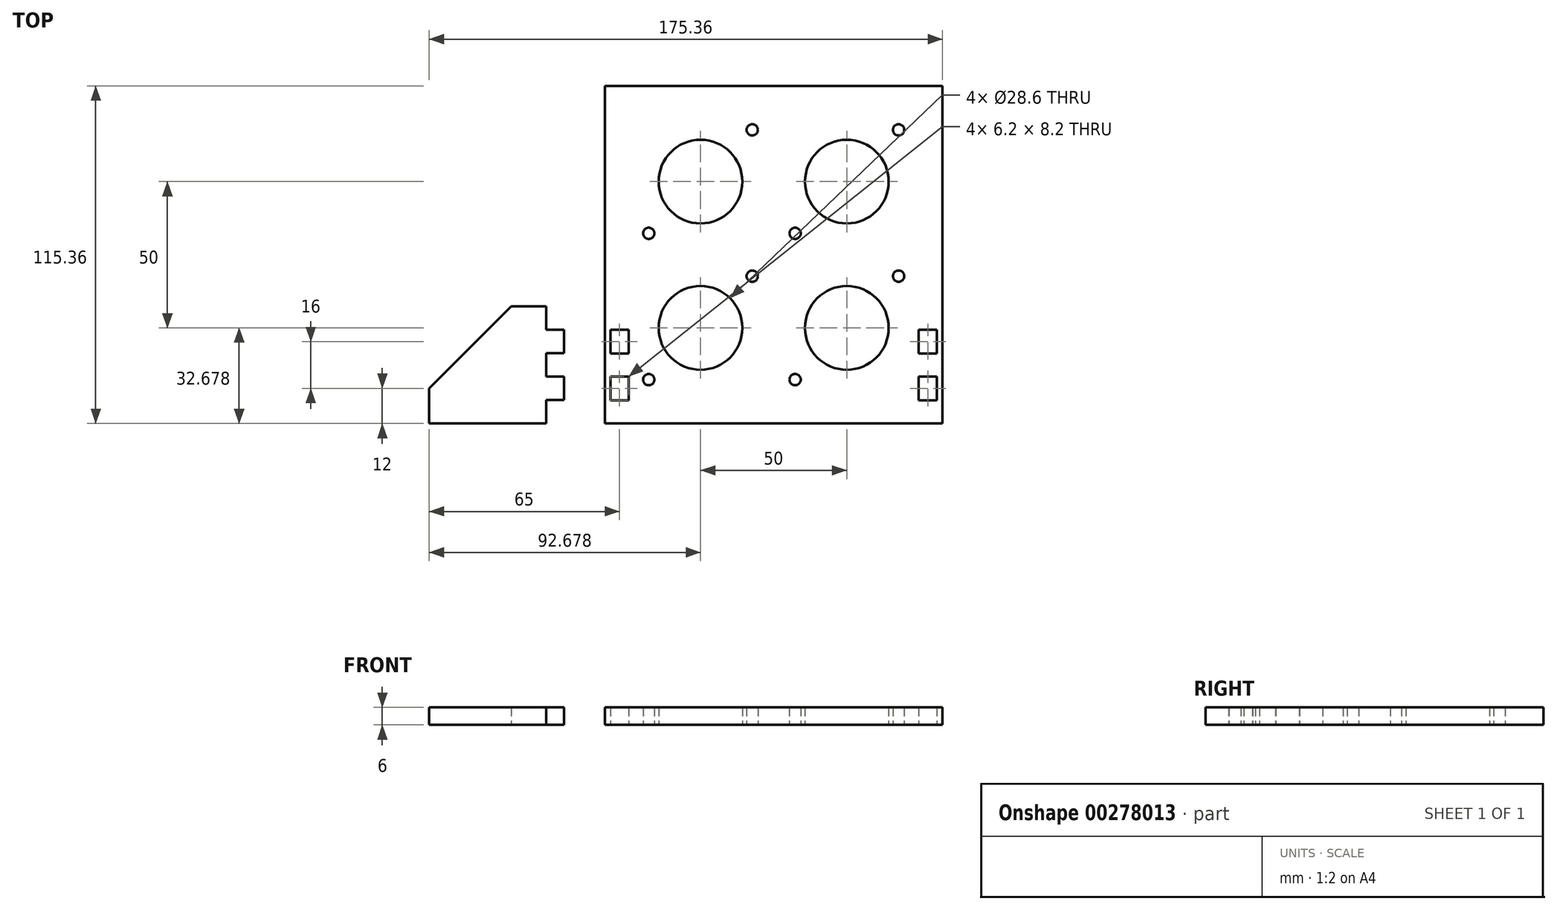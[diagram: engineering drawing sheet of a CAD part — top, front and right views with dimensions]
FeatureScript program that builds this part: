
annotation { "Feature Type Name" : "Feature", "Feature Type Description" : "" }
export const myFeature = defineFeature(function(context is Context, id is Id, definition is map)
    precondition{}
    {
        {
            assignVariable(context, id + "F0", {"name" : "X", "anyValue" : 6 * mm});
        }
        {
            var Q0;
            Q0=qCreatedBy(makeId("Top.planeOp"),FACE);
            var sketch = newSketch(context, id + "F1", { "sketchPlane" : qUnion([Q0])});
            skCircle(sketch, "E0", {"center": v(32.68, 32.68) * mm, "radius": 13.5 * mm, "construction": true});
            skCircle(sketch, "E1", {"center": v(15, 15) * mm, "radius": 1.93 * mm});
            skCircle(sketch, "E2", {"center": v(32.68, 32.68) * mm, "radius": 14.3 * mm});
            skCircle(sketch, "E3", {"center": v(50.36, 50.36) * mm, "radius": 1.93 * mm});
            skLineSegment(sketch, "E4", {"start": v(15, 15) * mm, "end": v(50.36, 50.36) * mm, "construction": true});
            skCircle(sketch, "E5.0.1.0", {"center": v(50.36, 100.36) * mm, "radius": 1.93 * mm});
            skCircle(sketch, "E5.0.1.1", {"center": v(32.68, 82.68) * mm, "radius": 14.3 * mm});
            skCircle(sketch, "E5.0.1.2", {"center": v(15, 65) * mm, "radius": 1.93 * mm});
            skCircle(sketch, "E5.1.0.0", {"center": v(100.36, 50.36) * mm, "radius": 1.93 * mm});
            skCircle(sketch, "E5.1.0.1", {"center": v(82.68, 32.68) * mm, "radius": 14.3 * mm});
            skCircle(sketch, "E5.1.0.2", {"center": v(65, 15) * mm, "radius": 1.93 * mm});
            skCircle(sketch, "E5.1.1.0", {"center": v(100.36, 100.36) * mm, "radius": 1.93 * mm});
            skCircle(sketch, "E5.1.1.1", {"center": v(82.68, 82.68) * mm, "radius": 14.3 * mm});
            skCircle(sketch, "E5.1.1.2", {"center": v(65, 65) * mm, "radius": 1.93 * mm});
            skLineSegment(sketch, "E5.direction1", {"start": v(15, 15) * mm, "end": v(65, 15) * mm, "construction": true});
            skLineSegment(sketch, "E5.direction2", {"start": v(15, 15) * mm, "end": v(15, 65) * mm, "construction": true});
            skLineSegment(sketch, "E6.bottom", {"start": v(0, 0) * mm, "end": v(115.36, 0) * mm});
            skLineSegment(sketch, "E7", {"start": v(100.36, 100.36) * mm, "end": v(100.36, 115.36) * mm, "construction": true});
            skLineSegment(sketch, "E8", {"start": v(100.36, 100.36) * mm, "end": v(115.36, 100.36) * mm, "construction": true});
            skLineSegment(sketch, "E9", {"start": v(15, 15) * mm, "end": v(0, 15) * mm, "construction": true});
            skLineSegment(sketch, "E10", {"start": v(15, 15) * mm, "end": v(15, 0) * mm, "construction": true});
            skLineSegment(sketch, "E11", {"start": v(-32, 40) * mm, "end": v(-60, 12) * mm});
            skLineSegment(sketch, "E12", {"start": v(-60, 12) * mm, "end": v(-60, 0) * mm});
            skLineSegment(sketch, "E13", {"start": v(-60, 0) * mm, "end": v(-20, 0) * mm});
            skLineSegment(sketch, "E14", {"start": v(-20, 0) * mm, "end": v(-20, 8) * mm});
            skLineSegment(sketch, "E15", {"start": v(-20, 40) * mm, "end": v(-32, 40) * mm});
            skLineSegment(sketch, "E16.trimOffspring", {"start": v(0, 0) * mm, "end": v(0, 115.36) * mm});
            skLineSegment(sketch, "E17", {"start": v(57.68, 115.36) * mm, "end": v(57.68, 0) * mm, "construction": true});
            skLineSegment(sketch, "E18", {"start": v(65, 10) * mm, "end": v(88.28, 10) * mm, "construction": true});
            skLineSegment(sketch, "E19", {"start": v(88.28, 10) * mm, "end": v(106.1, 27.82) * mm, "construction": true});
            skLineSegment(sketch, "E20", {"start": v(106.1, 27.82) * mm, "end": v(106.1, 51.1) * mm, "construction": true});
            skLineSegment(sketch, "E21", {"start": v(101.1, 56.1) * mm, "end": v(77.82, 56.1) * mm, "construction": true});
            skLineSegment(sketch, "E22", {"start": v(77.82, 56.1) * mm, "end": v(60, 38.28) * mm, "construction": true});
            skLineSegment(sketch, "E23", {"start": v(60, 38.28) * mm, "end": v(60, 15) * mm, "construction": true});
            skPoint(sketch, "E24.visualSharp", {"position": v(106.1, 56.1) * mm});
            skArc(sketch, "E24.filletArc", {"start": v(106.1, 51.1) * mm, "mid": v(104.64, 54.64) * mm, "end": v(101.1, 56.1) * mm, "construction": true});
            skPoint(sketch, "E25.visualSharp", {"position": v(60, 10) * mm});
            skArc(sketch, "E25.filletArc", {"start": v(60, 15) * mm, "mid": v(61.46, 11.46) * mm, "end": v(65, 10) * mm, "construction": true});
            skLineSegment(sketch, "E26", {"start": v(60, 10) * mm, "end": v(154.26, 104.26) * mm, "construction": true});
            skLineSegment(sketch, "E27", {"start": v(106.1, 56.1) * mm, "end": v(200.36, 150.36) * mm, "construction": true});
            skLineSegment(sketch, "E28", {"start": v(154.26, 104.26) * mm, "end": v(200.36, 150.36) * mm, "construction": true});
            skPoint(sketch, "E29", {"position": v(61.46, 11.46) * mm});
            skPoint(sketch, "E30", {"position": v(104.64, 54.64) * mm});
            skLineSegment(sketch, "E31.0.1.0", {"start": v(106.1, 77.82) * mm, "end": v(106.1, 101.1) * mm, "construction": true});
            skArc(sketch, "E31.0.1.1", {"start": v(106.1, 101.1) * mm, "mid": v(104.64, 104.64) * mm, "end": v(101.1, 106.1) * mm, "construction": true});
            skLineSegment(sketch, "E31.0.1.2", {"start": v(101.1, 106.1) * mm, "end": v(77.82, 106.1) * mm, "construction": true});
            skLineSegment(sketch, "E31.0.1.3", {"start": v(77.82, 106.1) * mm, "end": v(60, 88.28) * mm, "construction": true});
            skLineSegment(sketch, "E31.0.1.4", {"start": v(60, 88.28) * mm, "end": v(60, 65) * mm, "construction": true});
            skArc(sketch, "E31.0.1.5", {"start": v(60, 65) * mm, "mid": v(61.46, 61.46) * mm, "end": v(65, 60) * mm, "construction": true});
            skLineSegment(sketch, "E31.0.1.6", {"start": v(65, 60) * mm, "end": v(88.28, 60) * mm, "construction": true});
            skLineSegment(sketch, "E31.0.1.7", {"start": v(88.28, 60) * mm, "end": v(106.1, 77.82) * mm, "construction": true});
            skLineSegment(sketch, "E31.1.0.0", {"start": v(56.1, 27.82) * mm, "end": v(56.1, 51.1) * mm, "construction": true});
            skArc(sketch, "E31.1.0.1", {"start": v(56.1, 51.1) * mm, "mid": v(54.64, 54.64) * mm, "end": v(51.1, 56.1) * mm, "construction": true});
            skLineSegment(sketch, "E31.1.0.2", {"start": v(51.1, 56.1) * mm, "end": v(27.82, 56.1) * mm, "construction": true});
            skLineSegment(sketch, "E31.1.0.3", {"start": v(27.82, 56.1) * mm, "end": v(10, 38.28) * mm, "construction": true});
            skLineSegment(sketch, "E31.1.0.4", {"start": v(10, 38.28) * mm, "end": v(10, 15) * mm, "construction": true});
            skArc(sketch, "E31.1.0.5", {"start": v(10, 15) * mm, "mid": v(11.46, 11.46) * mm, "end": v(15, 10) * mm, "construction": true});
            skLineSegment(sketch, "E31.1.0.6", {"start": v(15, 10) * mm, "end": v(38.28, 10) * mm, "construction": true});
            skLineSegment(sketch, "E31.1.0.7", {"start": v(38.28, 10) * mm, "end": v(56.1, 27.82) * mm, "construction": true});
            skLineSegment(sketch, "E31.1.1.0", {"start": v(56.1, 77.82) * mm, "end": v(56.1, 101.1) * mm, "construction": true});
            skArc(sketch, "E31.1.1.1", {"start": v(56.1, 101.1) * mm, "mid": v(54.64, 104.64) * mm, "end": v(51.1, 106.1) * mm, "construction": true});
            skLineSegment(sketch, "E31.1.1.2", {"start": v(51.1, 106.1) * mm, "end": v(27.82, 106.1) * mm, "construction": true});
            skLineSegment(sketch, "E31.1.1.3", {"start": v(27.82, 106.1) * mm, "end": v(10, 88.28) * mm, "construction": true});
            skLineSegment(sketch, "E31.1.1.4", {"start": v(10, 88.28) * mm, "end": v(10, 65) * mm, "construction": true});
            skArc(sketch, "E31.1.1.5", {"start": v(10, 65) * mm, "mid": v(11.46, 61.46) * mm, "end": v(15, 60) * mm, "construction": true});
            skLineSegment(sketch, "E31.1.1.6", {"start": v(15, 60) * mm, "end": v(38.28, 60) * mm, "construction": true});
            skLineSegment(sketch, "E31.1.1.7", {"start": v(38.28, 60) * mm, "end": v(56.1, 77.82) * mm, "construction": true});
            skLineSegment(sketch, "E31.direction1", {"start": v(65, 10) * mm, "end": v(15, 10) * mm, "construction": true});
            skLineSegment(sketch, "E31.direction2", {"start": v(65, 10) * mm, "end": v(65, 60) * mm, "construction": true});
            skLineSegment(sketch, "E32.trimOffspring", {"start": v(0, 115.36) * mm, "end": v(115.36, 115.36) * mm});
            skLineSegment(sketch, "E33", {"start": v(115.36, 0) * mm, "end": v(115.36, 115.36) * mm});
            skLineSegment(sketch, "E34", {"start": v(-20, 32) * mm, "end": v(-14, 32) * mm});
            skLineSegment(sketch, "E35", {"start": v(-14, 32) * mm, "end": v(-14, 24) * mm});
            skLineSegment(sketch, "E36", {"start": v(-14, 24) * mm, "end": v(-20, 24) * mm});
            skLineSegment(sketch, "E37", {"start": v(-20, 16) * mm, "end": v(-14, 16) * mm});
            skLineSegment(sketch, "E38", {"start": v(-14, 16) * mm, "end": v(-14, 8) * mm});
            skLineSegment(sketch, "E39", {"start": v(-14, 8) * mm, "end": v(-20, 8) * mm});
            skLineSegment(sketch, "E40.trimOffspring", {"start": v(-20, 32) * mm, "end": v(-20, 40) * mm});
            skLineSegment(sketch, "E41.trimOffspring", {"start": v(-20, 16) * mm, "end": v(-20, 24) * mm});
            skLineSegment(sketch, "E42.bottom", {"start": v(2, 16) * mm, "end": v(8, 16) * mm, "construction": true});
            skLineSegment(sketch, "E42.top", {"start": v(2, 8) * mm, "end": v(8, 8) * mm, "construction": true});
            skLineSegment(sketch, "E42.left", {"start": v(2, 16) * mm, "end": v(2, 8) * mm, "construction": true});
            skLineSegment(sketch, "E42.right", {"start": v(8, 16) * mm, "end": v(8, 8) * mm, "construction": true});
            skLineSegment(sketch, "E43.bottom", {"start": v(2, 32) * mm, "end": v(8, 32) * mm, "construction": true});
            skLineSegment(sketch, "E43.top", {"start": v(2, 24) * mm, "end": v(8, 24) * mm, "construction": true});
            skLineSegment(sketch, "E43.left", {"start": v(2, 32) * mm, "end": v(2, 24) * mm, "construction": true});
            skLineSegment(sketch, "E43.right", {"start": v(8, 32) * mm, "end": v(8, 24) * mm, "construction": true});
            skLineSegment(sketch, "E44", {"start": v(10, 15.9) * mm, "end": v(8, 15.9) * mm, "construction": true});
            skLineSegment(sketch, "E45", {"start": v(2, 15.45) * mm, "end": v(0, 15.45) * mm, "construction": true});
            skLineSegment(sketch, "E46.0", {"start": v(1.9, 23.9) * mm, "end": v(8.1, 23.9) * mm});
            skLineSegment(sketch, "E46.1", {"start": v(1.9, 32.1) * mm, "end": v(1.9, 23.9) * mm});
            skLineSegment(sketch, "E46.2", {"start": v(1.9, 32.1) * mm, "end": v(8.1, 32.1) * mm});
            skLineSegment(sketch, "E46.3", {"start": v(8.1, 32.1) * mm, "end": v(8.1, 23.9) * mm});
            skLineSegment(sketch, "E47.0", {"start": v(1.9, 16.1) * mm, "end": v(1.9, 7.9) * mm});
            skLineSegment(sketch, "E47.1", {"start": v(1.9, 16.1) * mm, "end": v(8.1, 16.1) * mm});
            skLineSegment(sketch, "E47.2", {"start": v(8.1, 16.1) * mm, "end": v(8.1, 7.9) * mm});
            skLineSegment(sketch, "E47.3", {"start": v(1.9, 7.9) * mm, "end": v(8.1, 7.9) * mm});
            skLineSegment(sketch, "E48.MirrorCS", {"start": v(107.26, 32.1) * mm, "end": v(107.26, 23.9) * mm});
            skLineSegment(sketch, "E49.MirrorCS", {"start": v(113.46, 32.1) * mm, "end": v(107.26, 32.1) * mm});
            skLineSegment(sketch, "E50.MirrorCS", {"start": v(113.46, 32.1) * mm, "end": v(113.46, 23.9) * mm});
            skLineSegment(sketch, "E51.MirrorCS", {"start": v(113.46, 23.9) * mm, "end": v(107.26, 23.9) * mm});
            skLineSegment(sketch, "E52.MirrorCS", {"start": v(107.26, 16.1) * mm, "end": v(107.26, 7.9) * mm});
            skLineSegment(sketch, "E53.MirrorCS", {"start": v(113.46, 7.9) * mm, "end": v(107.26, 7.9) * mm});
            skLineSegment(sketch, "E54.MirrorCS", {"start": v(113.46, 16.1) * mm, "end": v(107.26, 16.1) * mm});
            skLineSegment(sketch, "E55.MirrorCS", {"start": v(113.46, 16.1) * mm, "end": v(113.46, 7.9) * mm});
            skSolve(sketch);
        }
        {
            var Q0;
            Q0=qSketchRegion(id+"F1",true);
            extrude(context, id + "F2", {"entities" : qUnion([Q0]), "depth" : getVariable(context, 'X')});
        }
    });
